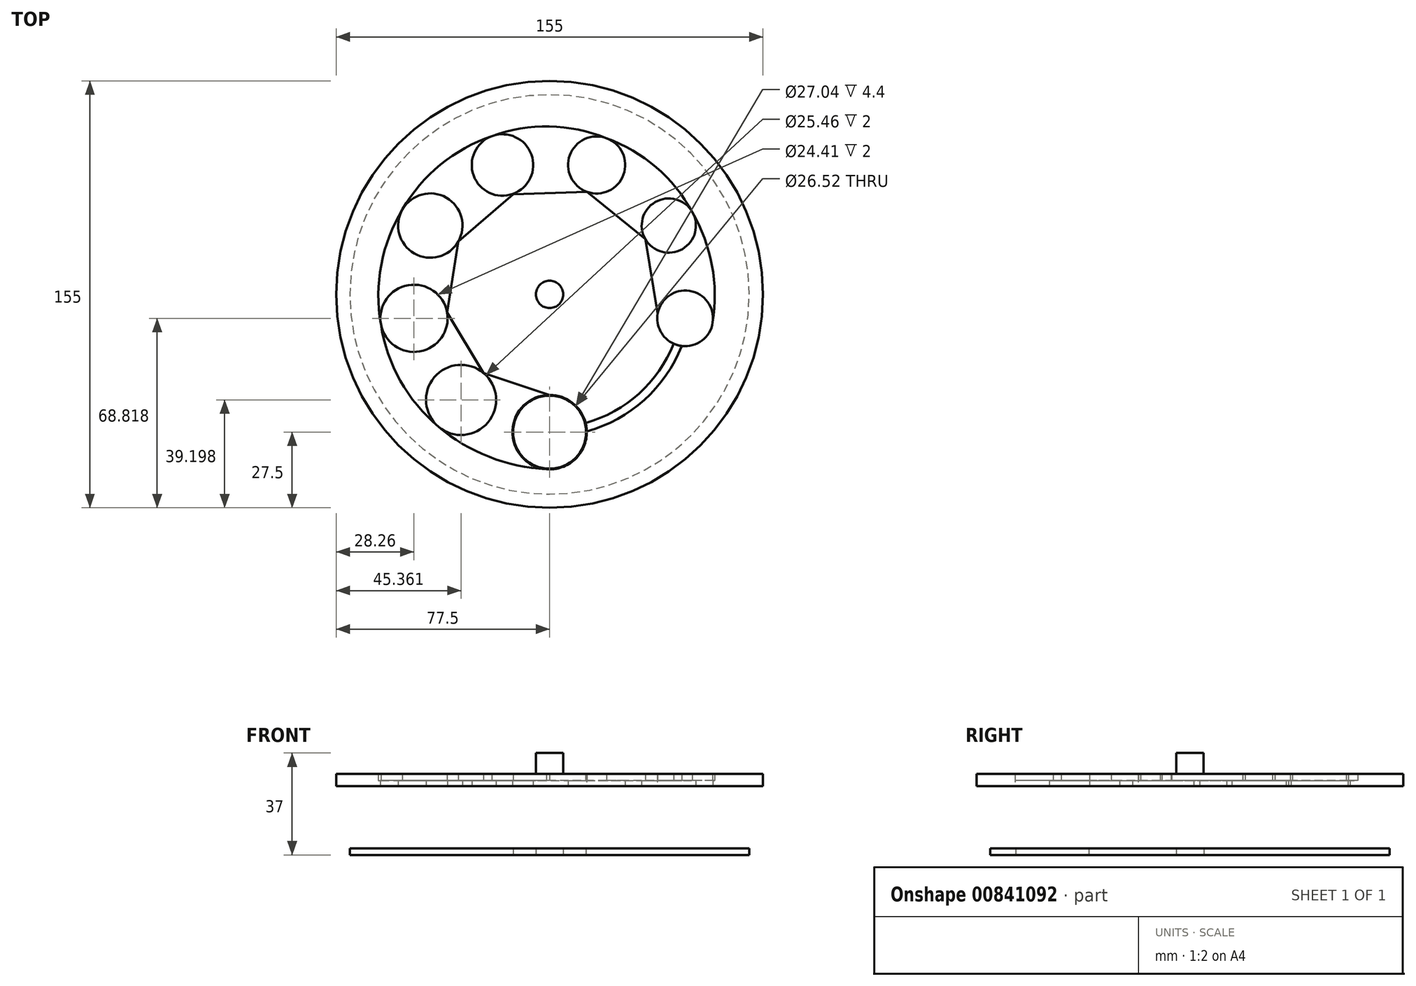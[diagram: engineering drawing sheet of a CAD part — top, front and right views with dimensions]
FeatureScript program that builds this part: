
annotation { "Feature Type Name" : "Feature", "Feature Type Description" : "" }
export const myFeature = defineFeature(function(context is Context, id is Id, definition is map)
    precondition{}
    {
        {
            var Q0;
            Q0=qCreatedBy(makeId("Top.planeOp"),FACE);
            var sketch = newSketch(context, id + "F0", { "sketchPlane" : qUnion([Q0])});
            skCircle(sketch, "E0", {"center": v(0, 0) * mm, "radius": 72.5 * mm});
            skCircle(sketch, "E1.cCircle", {"center": v(0, 0) * mm, "radius": 50 * mm, "construction": true});
            skLineSegment(sketch, "E1.0", {"start": v(-18.2, 50) * mm, "end": v(18.2, 50) * mm, "construction": true});
            skLineSegment(sketch, "E1.1", {"start": v(18.2, 50) * mm, "end": v(46.08, 26.6) * mm, "construction": true});
            skLineSegment(sketch, "E1.2", {"start": v(46.08, 26.6) * mm, "end": v(52.4, -9.24) * mm, "construction": true});
            skLineSegment(sketch, "E1.3", {"start": v(52.4, -9.24) * mm, "end": v(34.2, -40.76) * mm, "construction": true});
            skLineSegment(sketch, "E1.4", {"start": v(34.2, -40.76) * mm, "end": v(0, -53.2) * mm, "construction": true});
            skLineSegment(sketch, "E1.5", {"start": v(0, -53.2) * mm, "end": v(-34.2, -40.76) * mm, "construction": true});
            skLineSegment(sketch, "E1.6", {"start": v(-34.2, -40.76) * mm, "end": v(-52.4, -9.24) * mm, "construction": true});
            skLineSegment(sketch, "E1.7", {"start": v(-52.4, -9.24) * mm, "end": v(-46.08, 26.6) * mm, "construction": true});
            skLineSegment(sketch, "E1.8", {"start": v(-46.08, 26.6) * mm, "end": v(-18.2, 50) * mm, "construction": true});
            skPoint(sketch, "E1.0.midPoint", {"position": v(0, 50) * mm});
            skCircle(sketch, "E2", {"center": v(0, -50) * mm, "radius": 13.26 * mm});
            skLineSegment(sketch, "E3", {"start": v(0, -72.5) * mm, "end": v(0, -63.26) * mm, "construction": true});
            skLineSegment(sketch, "E4", {"start": v(-34.2, -40.76) * mm, "end": v(0, 0) * mm, "construction": true});
            skCircle(sketch, "E5", {"center": v(-32.14, -38.3) * mm, "radius": 13.26 * mm, "construction": true});
            skPoint(sketch, "E6", {"position": v(-20.94, -45.4) * mm});
            skPoint(sketch, "E7", {"position": v(-13.14, -48.24) * mm});
            skCircle(sketch, "E8", {"center": v(0, 0) * mm, "radius": 5 * mm});
            skSolve(sketch);
        }
        {
            var Q0;
            Q0=makeQuery(id+"F0.imprint","IMPRINT",FACE,{"disambiguationData":[TD([[makeQuery(id+"F0.imprint","IMPRINT",EDGE,{"derivedFrom":sQuery(id+"F0.wireOp",EDGE,"E0")}),1.0]])]});
            extrude(context, id + "F1", {"entities" : qUnion([Q0]), "depth" : 2.4 * mm, "offsetDistance" : 25 * mm});
        }
        {
            var Q0;
            Q0=qCreatedBy(makeId("Top.planeOp"),FACE);
            cPlane(context, id + "F2", {"entities" : qUnion([Q0]), "cplaneType" : CPlaneType.OFFSET, "offset" : 25 * mm, "width" : 150 * mm, "height" : 150 * mm});
        }
        {
            var Q0;
            Q0=qCreatedBy(id+"F2.planeOp",FACE);
            var sketch = newSketch(context, id + "F3", { "sketchPlane" : qUnion([Q0])});
            skCircle(sketch, "E9", {"center": v(0, 0) * mm, "radius": 77.5 * mm});
            skPoint(sketch, "E10", {"position": v(0, 72.5) * mm});
            skPoint(sketch, "E11", {"position": v(0, 77.5) * mm});
            skCircle(sketch, "E12.cCircle", {"center": v(0, 0) * mm, "radius": 77.5 * mm, "construction": true});
            skLineSegment(sketch, "E12.0", {"start": v(-28.2, 77.5) * mm, "end": v(28.2, 77.5) * mm, "construction": true});
            skLineSegment(sketch, "E12.1", {"start": v(28.2, 77.5) * mm, "end": v(71.42, 41.24) * mm, "construction": true});
            skLineSegment(sketch, "E12.2", {"start": v(71.42, 41.24) * mm, "end": v(81.22, -14.32) * mm, "construction": true});
            skLineSegment(sketch, "E12.3", {"start": v(81.22, -14.32) * mm, "end": v(53.01, -63.18) * mm, "construction": true});
            skLineSegment(sketch, "E12.4", {"start": v(53.01, -63.18) * mm, "end": v(0, -82.47) * mm, "construction": true});
            skLineSegment(sketch, "E12.5", {"start": v(0, -82.47) * mm, "end": v(-53.01, -63.18) * mm, "construction": true});
            skLineSegment(sketch, "E12.6", {"start": v(-53.01, -63.18) * mm, "end": v(-81.22, -14.32) * mm, "construction": true});
            skLineSegment(sketch, "E12.7", {"start": v(-81.22, -14.32) * mm, "end": v(-71.42, 41.24) * mm, "construction": true});
            skLineSegment(sketch, "E12.8", {"start": v(-71.42, 41.24) * mm, "end": v(-28.2, 77.5) * mm, "construction": true});
            skPoint(sketch, "E13", {"position": v(0, -50) * mm});
            skCircle(sketch, "E14", {"center": v(0, 0) * mm, "radius": 50 * mm, "construction": true});
            skLineSegment(sketch, "E15", {"start": v(0, 0) * mm, "end": v(-53.01, -63.18) * mm, "construction": true});
            skLineSegment(sketch, "E16", {"start": v(0, 0) * mm, "end": v(-81.22, -14.32) * mm, "construction": true});
            skLineSegment(sketch, "E17", {"start": v(0, 0) * mm, "end": v(-71.42, 41.24) * mm, "construction": true});
            skLineSegment(sketch, "E18", {"start": v(0, 0) * mm, "end": v(-28.2, 77.5) * mm, "construction": true});
            skLineSegment(sketch, "E19", {"start": v(0, 0) * mm, "end": v(28.2, 77.5) * mm, "construction": true});
            skLineSegment(sketch, "E20", {"start": v(71.42, 41.24) * mm, "end": v(0, 0) * mm, "construction": true});
            skLineSegment(sketch, "E21", {"start": v(81.22, -14.32) * mm, "end": v(0, 0) * mm, "construction": true});
            skCircle(sketch, "E22", {"center": v(0, -50) * mm, "radius": 13.52 * mm});
            skCircle(sketch, "E23", {"center": v(-32.14, -38.3) * mm, "radius": 12.73 * mm});
            skCircle(sketch, "E24", {"center": v(-49.24, -8.68) * mm, "radius": 12.2 * mm});
            skCircle(sketch, "E25", {"center": v(-43.3, 25) * mm, "radius": 11.68 * mm});
            skCircle(sketch, "E26", {"center": v(-17.1, 46.98) * mm, "radius": 11.16 * mm});
            skCircle(sketch, "E27", {"center": v(17.1, 46.98) * mm, "radius": 10.37 * mm});
            skCircle(sketch, "E28", {"center": v(43.3, 25) * mm, "radius": 9.84 * mm});
            skCircle(sketch, "E29", {"center": v(49.24, -8.68) * mm, "radius": 10.1 * mm});
            skSolve(sketch);
        }
        {
            var Q0;
            Q0=makeQuery(id+"F3.imprint","IMPRINT",FACE,{"disambiguationData":[TD([[makeQuery(id+"F3.imprint","IMPRINT",EDGE,{"derivedFrom":sQuery(id+"F3.wireOp",EDGE,"E9")}),1.0]])]});
            extrude(context, id + "F4", {"entities" : qUnion([Q0]), "depth" : 2 * mm, "offsetDistance" : 25 * mm});
        }
        {
            var Q0;
            Q0=makeQuery(id+"F4.opExtrude","CAP_FACE",FACE,{"disambiguationData":[OSD([sQuery(id+"F3.wireOp",EDGE,"E9"),sQuery(id+"F3.wireOp",EDGE,"E22"),sQuery(id+"F3.wireOp",EDGE,"E23"),sQuery(id+"F3.wireOp",EDGE,"E24"),sQuery(id+"F3.wireOp",EDGE,"E25"),sQuery(id+"F3.wireOp",EDGE,"E26"),sQuery(id+"F3.wireOp",EDGE,"E27"),sQuery(id+"F3.wireOp",EDGE,"E28"),sQuery(id+"F3.wireOp",EDGE,"E29")])],"isStart":false});
            var sketch = newSketch(context, id + "F5", { "sketchPlane" : qUnion([Q0])});
            skCircle(sketch, "E30", {"center": v(0, 0) * mm, "radius": 4.95 * mm});
            skSolve(sketch);
        }
        {
            var Q0;
            Q0=makeQuery(id+"F5.imprint","IMPRINT",FACE,{"disambiguationData":[TD([[makeQuery(id+"F5.imprint","IMPRINT",EDGE,{"derivedFrom":sQuery(id+"F5.wireOp",EDGE,"E30")}),1.0]])]});
            extrude(context, id + "F6", {"entities" : qUnion([Q0]), "operationType" : NewBodyOperationType.ADD, "depth" : 10 * mm, "offsetDistance" : 25 * mm});
        }
        {
            var Q0;
            Q0=makeQuery(id+"F4.opExtrude","CAP_FACE",FACE,{"disambiguationData":[OSD([sQuery(id+"F3.wireOp",EDGE,"E9"),sQuery(id+"F3.wireOp",EDGE,"E22"),sQuery(id+"F3.wireOp",EDGE,"E23"),sQuery(id+"F3.wireOp",EDGE,"E24"),sQuery(id+"F3.wireOp",EDGE,"E25"),sQuery(id+"F3.wireOp",EDGE,"E26"),sQuery(id+"F3.wireOp",EDGE,"E27"),sQuery(id+"F3.wireOp",EDGE,"E28"),sQuery(id+"F3.wireOp",EDGE,"E29")])],"isStart":false});
            var sketch = newSketch(context, id + "F7", { "sketchPlane" : qUnion([Q0])});
            skPoint(sketch, "E31", {"position": v(0, -50) * mm});
            skPoint(sketch, "E32", {"position": v(-32.14, -38.3) * mm});
            skPoint(sketch, "E33", {"position": v(-49.24, -8.68) * mm});
            skPoint(sketch, "E34", {"position": v(-43.3, 25) * mm});
            skPoint(sketch, "E35", {"position": v(-17.1, 46.98) * mm});
            skPoint(sketch, "E36", {"position": v(17.1, 46.98) * mm});
            skPoint(sketch, "E37", {"position": v(43.3, 25) * mm});
            skPoint(sketch, "E38", {"position": v(49.24, -8.68) * mm});
            skLineSegment(sketch, "E39", {"start": v(0, 0) * mm, "end": v(76.32, -13.46) * mm, "construction": true});
            skLineSegment(sketch, "E40", {"start": v(0, 0) * mm, "end": v(67.12, 38.75) * mm, "construction": true});
            skLineSegment(sketch, "E41", {"start": v(0, 0) * mm, "end": v(26.5, 72.83) * mm, "construction": true});
            skLineSegment(sketch, "E42", {"start": v(0, 0) * mm, "end": v(-26.5, 72.83) * mm, "construction": true});
            skLineSegment(sketch, "E43", {"start": v(0, 0) * mm, "end": v(-67.12, 38.75) * mm, "construction": true});
            skLineSegment(sketch, "E44", {"start": v(0, 0) * mm, "end": v(-76.32, -13.46) * mm, "construction": true});
            skLineSegment(sketch, "E45", {"start": v(0, 0) * mm, "end": v(-49.82, -59.37) * mm, "construction": true});
            skLineSegment(sketch, "E46", {"start": v(0, 0) * mm, "end": v(0, -77.5) * mm, "construction": true});
            skPoint(sketch, "E47", {"position": v(39.29, -6.93) * mm});
            skPoint(sketch, "E48", {"position": v(34.78, 20.08) * mm});
            skPoint(sketch, "E49", {"position": v(13.55, 37.24) * mm});
            skPoint(sketch, "E50", {"position": v(-13.25, 36.51) * mm});
            skPoint(sketch, "E50.positionSnap0", {"position": v(-13.25, 36.41) * mm});
            skPoint(sketch, "E51", {"position": v(-33.19, 19.16) * mm});
            skPoint(sketch, "E52", {"position": v(-37.22, -6.56) * mm});
            skPoint(sketch, "E53", {"position": v(-23.96, -28.55) * mm});
            skPoint(sketch, "E54", {"position": v(0, -36.48) * mm});
            skLineSegment(sketch, "E55", {"start": v(0, -36.48) * mm, "end": v(-23.96, -28.55) * mm});
            skLineSegment(sketch, "E56", {"start": v(-23.96, -28.55) * mm, "end": v(-37.22, -6.56) * mm});
            skLineSegment(sketch, "E57", {"start": v(-37.22, -6.56) * mm, "end": v(-33.19, 19.16) * mm});
            skLineSegment(sketch, "E58", {"start": v(-33.19, 19.16) * mm, "end": v(-13.25, 36.41) * mm});
            skLineSegment(sketch, "E59", {"start": v(-13.25, 36.41) * mm, "end": v(13.55, 37.24) * mm});
            skLineSegment(sketch, "E60", {"start": v(13.55, 37.24) * mm, "end": v(34.78, 20.08) * mm});
            skLineSegment(sketch, "E61", {"start": v(34.78, 20.08) * mm, "end": v(39.29, -6.93) * mm});
            skArc(sketch, "E62", {"start": v(59.2, -10.44) * mm, "mid": v(59, 10.38) * mm, "end": v(51.83, 29.92) * mm});
            skArc(sketch, "E63", {"start": v(13.1, -46.7) * mm, "mid": v(32.46, -36.03) * mm, "end": v(45.08, -17.9) * mm});
            skArc(sketch, "E64", {"start": v(13.52, -49.7) * mm, "mid": v(34.43, -38.3) * mm, "end": v(47.98, -18.7) * mm});
            skArc(sketch, "E65", {"start": v(13.4, -48.17) * mm, "mid": v(37.02, -33.6) * mm, "end": v(49.24, -8.68) * mm, "construction": true});
            skArc(sketch, "E66", {"start": v(13.1, -46.7) * mm, "mid": v(8.3, -39.34) * mm, "end": v(0, -36.48) * mm});
            skArc(sketch, "E67", {"start": v(39.29, -6.93) * mm, "mid": v(40.3, -13.4) * mm, "end": v(45.08, -17.9) * mm});
            skArc(sketch, "E68", {"start": v(47.98, -18.7) * mm, "mid": v(55.24, -16.81) * mm, "end": v(59.2, -10.44) * mm});
            skArc(sketch, "E69", {"start": v(-40.32, -48.05) * mm, "mid": v(-21.46, -59.16) * mm, "end": v(0, -63.52) * mm});
            skArc(sketch, "E70", {"start": v(0, -63.52) * mm, "mid": v(9.67, -59.45) * mm, "end": v(13.52, -49.7) * mm});
            skArc(sketch, "E71", {"start": v(-61.26, -10.8) * mm, "mid": v(-54.19, -31.34) * mm, "end": v(-40.32, -48.05) * mm});
            skArc(sketch, "E72", {"start": v(-53.42, 30.84) * mm, "mid": v(-61.14, 10.73) * mm, "end": v(-61.26, -10.8) * mm});
            skArc(sketch, "E73", {"start": v(-20.92, 57.47) * mm, "mid": v(-39.6, 47.12) * mm, "end": v(-53.42, 30.84) * mm});
            skArc(sketch, "E74", {"start": v(20.65, 56.73) * mm, "mid": v(-0.07, 60.95) * mm, "end": v(-20.92, 57.47) * mm});
            skArc(sketch, "E75", {"start": v(51.83, 29.92) * mm, "mid": v(38.68, 46.17) * mm, "end": v(20.65, 56.73) * mm});
            skSolve(sketch);
        }
        {
            var Q0;
            Q0=makeQuery(id+"F7.imprint","IMPRINT",FACE,{"disambiguationData":[TD([[makeQuery(id+"F7.imprint","IMPRINT",EDGE,{"derivedFrom":sQuery(id+"F7.wireOp",EDGE,"E64")}),-1.0]])]});
            var Q1;
            Q1=makeQuery(id+"F7.imprint","IMPRINT",FACE,{"disambiguationData":[TD([[makeQuery(id+"F7.imprint","IMPRINT",EDGE,{"derivedFrom":sQuery(id+"F7.wireOp",EDGE,"E55")}),-1.0]])]});
            extrude(context, id + "F8", {"entities" : qUnion([Q0, Q1]), "operationType" : NewBodyOperationType.ADD, "depth" : 2.4 * mm, "offsetDistance" : 25 * mm});
        }
    });
